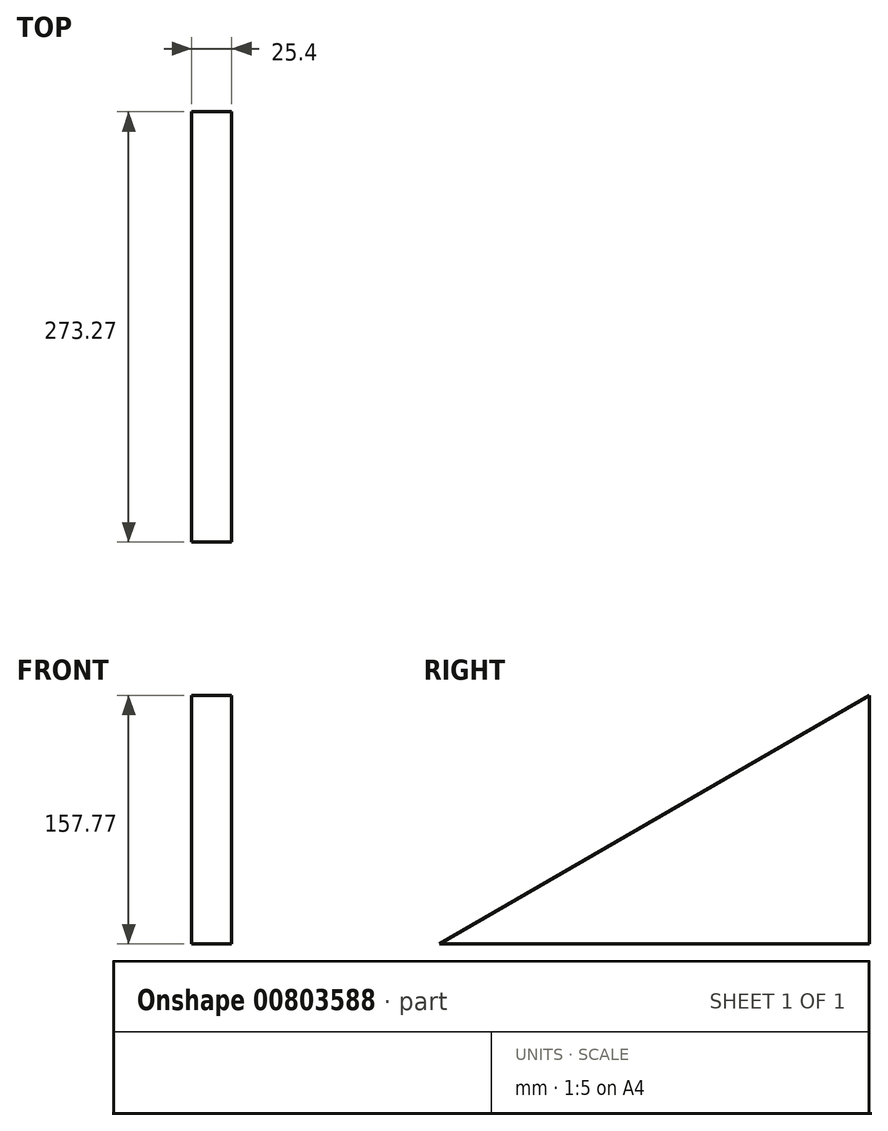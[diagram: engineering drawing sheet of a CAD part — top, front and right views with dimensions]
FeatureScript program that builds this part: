
annotation { "Feature Type Name" : "Feature", "Feature Type Description" : "" }
export const myFeature = defineFeature(function(context is Context, id is Id, definition is map)
    precondition{}
    {
        {
            var Q0;
            Q0=qCreatedBy(makeId("Right.planeOp"),FACE);
            var sketch = newSketch(context, id + "F0", { "sketchPlane" : qUnion([Q0])});
            skLineSegment(sketch, "E0", {"start": v(-273.27, 0) * mm, "end": v(0, 157.77) * mm});
            skLineSegment(sketch, "E1", {"start": v(-273.27, 0) * mm, "end": v(0, 0) * mm});
            skLineSegment(sketch, "E2", {"start": v(0, 0) * mm, "end": v(0, 157.77) * mm});
            skSolve(sketch);
        }
        {
            var Q0;
            Q0 = qSketchRegion(id + "F0", true);
            extrude(context, id + "F1", {"entities" : qUnion([Q0]), "endBound" : BoundingType.SYMMETRIC, "depth" : 25.4 * mm, "offsetDistance" : 25.4 * mm});
        }
    });
